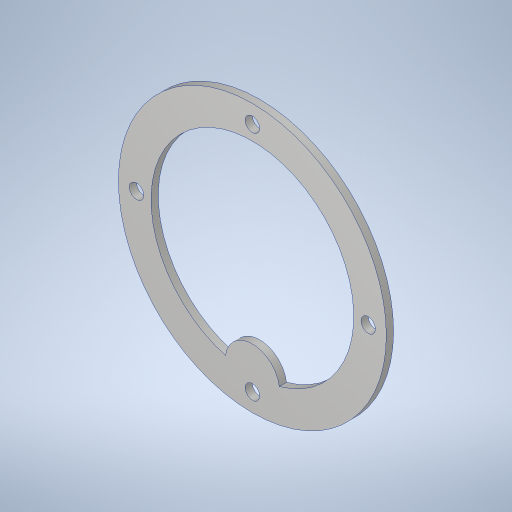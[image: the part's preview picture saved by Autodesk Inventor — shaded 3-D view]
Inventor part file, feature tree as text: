
AUTODESK INVENTOR PART (.ipt)
format: ipt  version: 2023.4 (Build 274418000, 418)  size: 262,144 bytes
history: native  units: in
note: dims shown in document units (in); Inventor stores cm internally (conversion verified against a paired STEP export)
features: extrude x1, sketch x1
ambient origin geometry x8: Origin, YZ Plane, XZ Plane, XY Plane, X Axis, Y Axis, Z Axis, Center Point
bodies: Solid1 (feature_tree)
feature tree (2):
  extrude  "Extrusion1"  Depth=0.1in
  sketch  "Sketch1"  dims[d0=2.8in d1=3.7in d2=0.75in d6=1.5748in d8=360.0deg d10=0.1in d11=0.0in d12=0.201in d13=0.25in]
